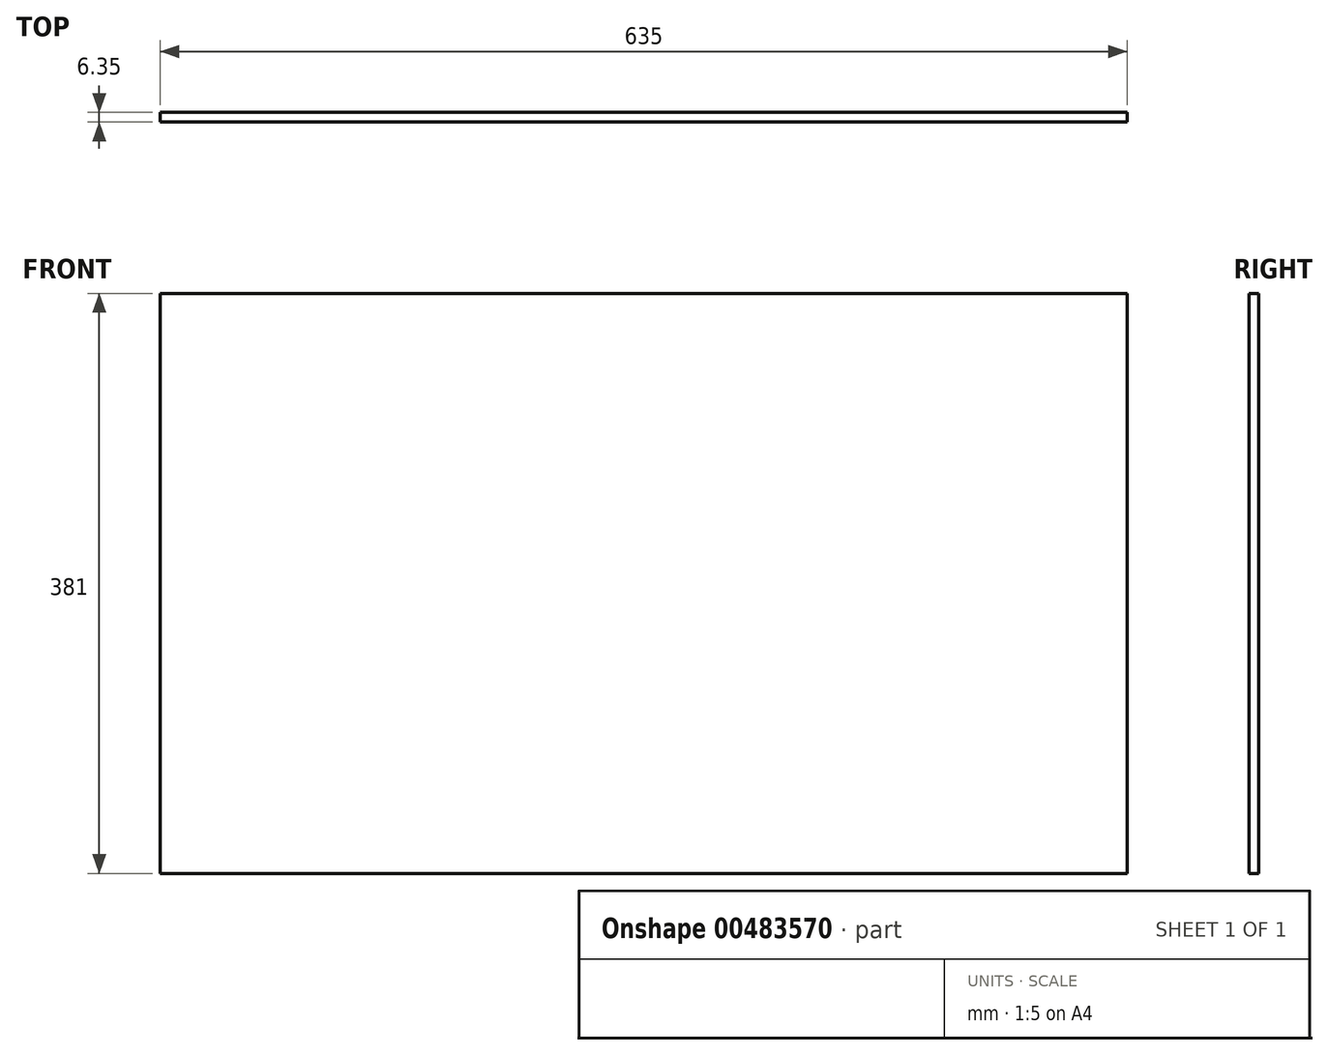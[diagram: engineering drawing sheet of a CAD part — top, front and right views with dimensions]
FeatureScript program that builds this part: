
annotation { "Feature Type Name" : "Feature", "Feature Type Description" : "" }
export const myFeature = defineFeature(function(context is Context, id is Id, definition is map)
    precondition{}
    {
        {
            var Q0;
            Q0=qCreatedBy(makeId("Front.planeOp"),FACE);
            var sketch = newSketch(context, id + "F0", { "sketchPlane" : qUnion([Q0])});
            skLineSegment(sketch, "E0.bottom", {"start": v(-459.88, -203.76) * mm, "end": v(175.12, -203.76) * mm});
            skLineSegment(sketch, "E0.top", {"start": v(-459.88, 177.24) * mm, "end": v(175.12, 177.24) * mm});
            skLineSegment(sketch, "E0.left", {"start": v(-459.88, -203.76) * mm, "end": v(-459.88, 177.24) * mm});
            skLineSegment(sketch, "E0.right", {"start": v(175.12, -203.76) * mm, "end": v(175.12, 177.24) * mm});
            skPoint(sketch, "E1.endSnap0", {"position": v(175.12, -13.26) * mm});
            skSolve(sketch);
        }
        {
            var Q0;
            Q0=makeQuery(id+"F0.imprint","IMPRINT",FACE,{"disambiguationData":[TD([[makeQuery(id+"F0.imprint","IMPRINT",EDGE,{"derivedFrom":sQuery(id+"F0.wireOp",EDGE,"E0.bottom")}),1.0]])]});
            extrude(context, id + "F1", {"entities" : qUnion([Q0]), "depth" : 6.35 * mm});
        }
    });
